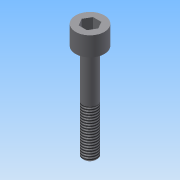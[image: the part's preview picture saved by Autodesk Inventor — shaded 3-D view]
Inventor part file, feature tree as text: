
AUTODESK INVENTOR PART (.ipt)
format: ipt  version: 2015 (Build 190159000, 159)  size: 96,256 bytes
history: native  units: mm
features: extrude x3, sketch x3, thread x1, chamfer x1
ambient origin geometry x8: Origin, YZ Plane, XZ Plane, XY Plane, X Axis, Y Axis, Z Axis, Center Point
bodies: 实体1 (feature_tree)
feature tree (8):
  extrude  "拉伸1"  Depth=4.0mm TaperAngle=0.0deg
  extrude  "拉伸2"  Depth=2.5mm TaperAngle=0.0deg
  extrude  "拉伸3"  Depth=20.0mm TaperAngle=0.0deg
  thread  "螺纹1"  [1 undecoded]
  chamfer  "倒角1"  Distance=0.25mm Angle=45.0deg
  sketch  "草图1"  dims[d0=6.0mm d1=4.0mm d2=0.0mm]
  sketch  "草图2"  dims[d3=3.0mm d4=2.5mm d5=0.0mm]
  sketch  "草图3"  dims[d6=3.0mm d7=20.0mm d8=0.0mm d9=10.0mm d10=0.0mm d11=0.25mm d12=2.0mm d13=45.0deg]
note: 1 required parameter value undecoded (feature->parameter linkage not recoverable at this tier; creation-order binding heuristic only, values carry confidence <= 0.55)
